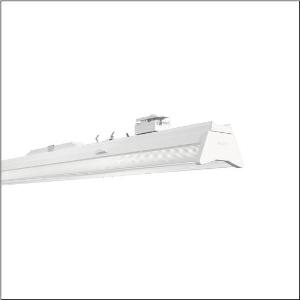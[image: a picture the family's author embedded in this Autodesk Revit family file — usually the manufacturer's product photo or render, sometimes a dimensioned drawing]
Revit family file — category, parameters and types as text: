
# Revit family: licross_r__11_performance_ho_51tm16dn4fxm_a8d0
name_source: partatom
category: Lighting Fixtures
units: mm (PartAtom-declared; Revit-internal decimal feet)

## family parameters
Cut with Voids When Loaded = No
Host = Face
Light Source = No
Part Type = Normal
Room Calculation Point = No
Round Connector Dimension = Use Diameter
Shared = No

## types (1)
- --- (1 x LED, 15460 lm, 87.3 W, 4000K)
    Apparent Load = 87 VA
    CIE Flux Codes = 63 87 95 78 100
    Color Rendering = 80
    Color Temperature = 4000K
    Default Elevation = 1800 mm
    Description = Licross® 11 Performance HO, luminaire insert, of sheet steel, galvanised, coil coated, white, length: 1.500mm, width: 120mm, height: 123mm, LED rated luminous flux: 15.460lm, light colour: 840, control gear: DALI 2, with plug, 5-pole, with phase selection, mains connection: 220..240V, AC, 50/60Hz, rated input power: 87W, halogen-free wiring, primary light control with lens, of plastic, primary optical cover: cover, of PMMA, light emission: direct/indirect distribution, primary light characteristic: symmetric, protection rating (complete): IP40, insulation class (complete): insulation class I (protective earthing), certification: CE, ENEC, VDE, UKCA, protection symbol: D if used in an environment without relevant dust loads with corresponding accessories, impact resistance: IK06, permissible ambient temperature for indoor applications: -25..+30°C, corresponds to IFS (International Featured Standards) requirements for safety and quality in the food industry, reducing of maximum allowable ambient temperature of 5°C with ceiling mounting, LABS conformity tested according to VDMA 24364:2018-05, packaging unit: 1 piece
    Height = 114 mm
    Lamp = 1 x LED
    Lamp Light Flux = 15460 lm
    Lamp Power = 87.3 W
    Lamp count = 1
    Length = 1500 mm
    Luminous efficacy = 177 lm/W
    Manufacturer = Siteco
    ModVariant = No
    Model = 51TM16DN4FXM
    Mounting Place = Ceiling
    Mounting Type = Pendant
    Number of Poles = 1
    OnlyDefault = Yes
    Power Factor = 1
    Product Name = Licross® 11 Performance HO
    Product group = luminaire insert
    ProductGroupID = 901
    Protection Class = Protection class I
    Protection Degree = IP 40
    RLX_Detail_Level = 1
    RLX_Emergency_Light_Flux = 0 lm
    RLX_Emergency_Type = 0
    RLX_Emergency_Type_DB = No
    RlxData = <blob elided: 34093 chars, md5=cfffd60b>
    Socket = socket
    Standby Power = 0 W
    System Light Flux = 15460 lm
    System Power = 87 W
    Type Comments = factory setting: luminous flux: 100 % | dim-lin: 254 | 589 mA
    Type Image = l_1256138.jpg
    URL = http://relux.com
    VarID = @adj_049677
    Voltage = 0 V
    Weight = 0.00 kg
    Width = 120 mm

## geometry (parser evidence)
native form markers: Blend x4, Sweep x9
no freeform markers — native parametric forms only
